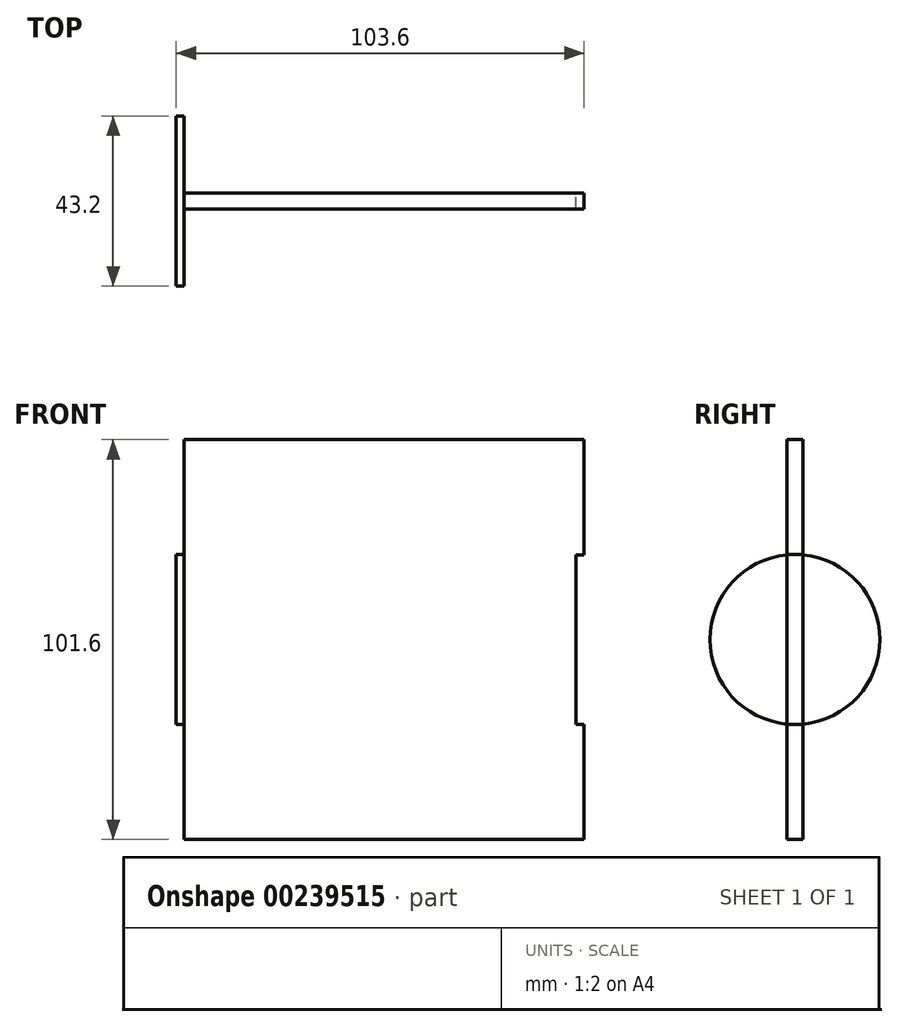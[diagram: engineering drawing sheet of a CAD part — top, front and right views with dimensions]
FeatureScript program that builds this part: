
annotation { "Feature Type Name" : "Feature", "Feature Type Description" : "" }
export const myFeature = defineFeature(function(context is Context, id is Id, definition is map)
    precondition{}
    {
        {
            assignVariable(context, id + "F0", {"name" : "P", "anyValue" : 4});
        }
        {
            var Q0;
            Q0=qCreatedBy(makeId("Front.planeOp"),FACE);
            var sketch = newSketch(context, id + "F1", { "sketchPlane" : qUnion([Q0])});
            skLineSegment(sketch, "E0.bottom", {"start": v(-50.8, 50.8) * mm, "end": v(50.8, 50.8) * mm});
            skLineSegment(sketch, "E0.top", {"start": v(-50.8, -50.8) * mm, "end": v(50.8, -50.8) * mm});
            skLineSegment(sketch, "E0.left", {"start": v(-50.8, 50.8) * mm, "end": v(-50.8, -50.8) * mm});
            skLineSegment(sketch, "E0.right", {"start": v(50.8, 50.8) * mm, "end": v(50.8, -50.8) * mm});
            skPoint(sketch, "E0.middle", {"position": v(0, 0) * mm});
            skSolve(sketch);
        }
        {
            var Q0;
            Q0=makeQuery(id+"F1.imprint","IMPRINT",FACE,{"disambiguationData":[TD([[makeQuery(id+"F1.imprint","IMPRINT",EDGE,{"derivedFrom":sQuery(id+"F1.wireOp",EDGE,"E0.bottom")}),-1.0]])]});
            extrude(context, id + "F2", {"entities" : qUnion([Q0]), "endBound" : BoundingType.SYMMETRIC, "depth" : (getVariable(context, 'P')) * mm});
        }
        {
            var Q0;
            Q0=makeQuery(id+"F2.opExtrude","SWEPT_FACE",FACE,{"disambiguationData":[OSD([sQuery(id+"F1.wireOp",EDGE,"E0.right")])]});
            var sketch = newSketch(context, id + "F3", { "sketchPlane" : qUnion([Q0])});
            skCircle(sketch, "E1", {"center": v(0, 0) * mm, "radius": 21.6 * mm});
            skSolve(sketch);
        }
        {
            var Q0;
            Q0 = qSketchRegion(id + "F3", true);
            extrude(context, id + "F4", {"entities" : qUnion([Q0]), "operationType" : NewBodyOperationType.REMOVE, "oppositeDirection" : true, "depth" : (((getVariable(context, 'P')) / 2)) * mm});
        }
        {
            var Q0;
            Q0=makeQuery(id+"F2.opExtrude","SWEPT_FACE",FACE,{"disambiguationData":[OSD([sQuery(id+"F1.wireOp",EDGE,"E0.left")])]});
            var sketch = newSketch(context, id + "F5", { "sketchPlane" : qUnion([Q0])});
            skCircle(sketch, "E2.0", {"center": v(0, 0) * mm, "radius": 21.6 * mm});
            skSolve(sketch);
        }
        {
            var Q0;
            Q0 = qSketchRegion(id + "F5", true);
            extrude(context, id + "F6", {"entities" : qUnion([Q0]), "operationType" : NewBodyOperationType.ADD, "depth" : (((getVariable(context, 'P')) / 2)) * mm});
        }
    });
